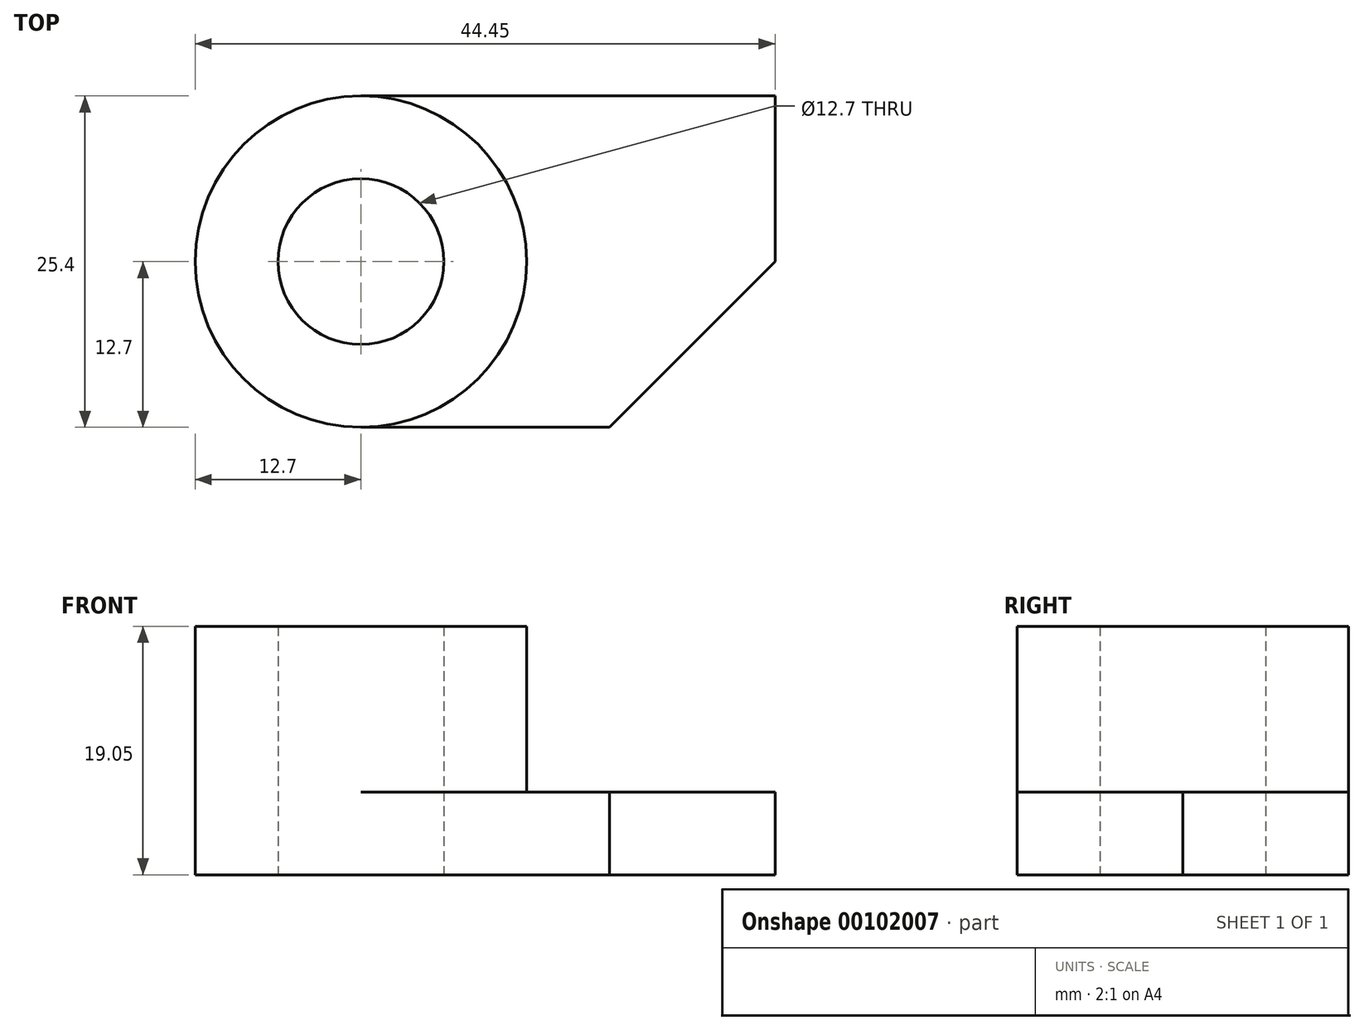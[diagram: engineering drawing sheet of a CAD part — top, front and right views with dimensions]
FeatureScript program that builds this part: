
annotation { "Feature Type Name" : "Feature", "Feature Type Description" : "" }
export const myFeature = defineFeature(function(context is Context, id is Id, definition is map)
    precondition{}
    {
        {
            var Q0;
            Q0=qCreatedBy(makeId("Top.planeOp"),FACE);
            var sketch = newSketch(context, id + "F0", { "sketchPlane" : qUnion([Q0])});
            skCircle(sketch, "E0", {"center": v(0, 0) * mm, "radius": 6.35 * mm});
            skCircle(sketch, "E1", {"center": v(0, 0) * mm, "radius": 12.7 * mm});
            skSolve(sketch);
        }
        {
            var Q0;
            Q0 = qSketchRegion(id + "F0", true);
            extrude(context, id + "F1", {"entities" : qUnion([Q0]), "depth" : 19.05 * mm});
        }
        {
            var Q0;
            Q0=qCreatedBy(makeId("Top.planeOp"),FACE);
            var sketch = newSketch(context, id + "F2", { "sketchPlane" : qUnion([Q0])});
            skLineSegment(sketch, "E2", {"start": v(0, 12.7) * mm, "end": v(31.75, 12.7) * mm});
            skLineSegment(sketch, "E3", {"start": v(31.75, 12.7) * mm, "end": v(31.75, 0) * mm});
            skLineSegment(sketch, "E4", {"start": v(31.75, 0) * mm, "end": v(19.05, -12.7) * mm});
            skLineSegment(sketch, "E5", {"start": v(19.05, -12.7) * mm, "end": v(0, -12.7) * mm});
            skArc(sketch, "E6", {"start": v(0, -12.7) * mm, "mid": v(12.7, 0) * mm, "end": v(0, 12.7) * mm});
            skSolve(sketch);
        }
        {
            var Q0;
            Q0 = qSketchRegion(id + "F2", true);
            extrude(context, id + "F3", {"entities" : qUnion([Q0]), "operationType" : NewBodyOperationType.ADD, "depth" : 6.35 * mm});
        }
    });
